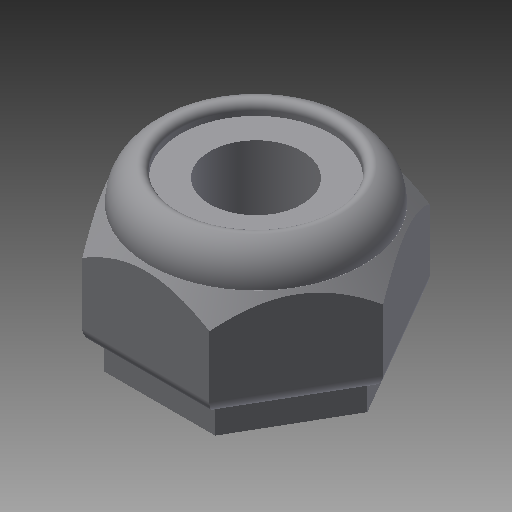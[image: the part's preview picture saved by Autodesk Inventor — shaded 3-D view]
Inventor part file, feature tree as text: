
AUTODESK INVENTOR PART (.ipt)
format: ipt  version: 2017 (Build 210142000, 142)  size: 172,544 bytes
history: native  units: in
note: dims shown in document units (in); Inventor stores cm internally (conversion verified against a paired STEP export)
features: extrude x1, other x1, imported_body x1
ambient origin geometry x8: Origin, YZ Plane, XZ Plane, XY Plane, X Axis, Y Axis, Z Axis, Center Point
bodies: Body1 (feature_tree)
feature tree (3):
  extrude  "Extrude1"  [1 undecoded]
  other  "NUT-832-NYLOCK.ipt1"
  imported_body  "Base1"
note: 1 required parameter value undecoded (feature->parameter linkage not recoverable at this tier; creation-order binding heuristic only, values carry confidence <= 0.55)
